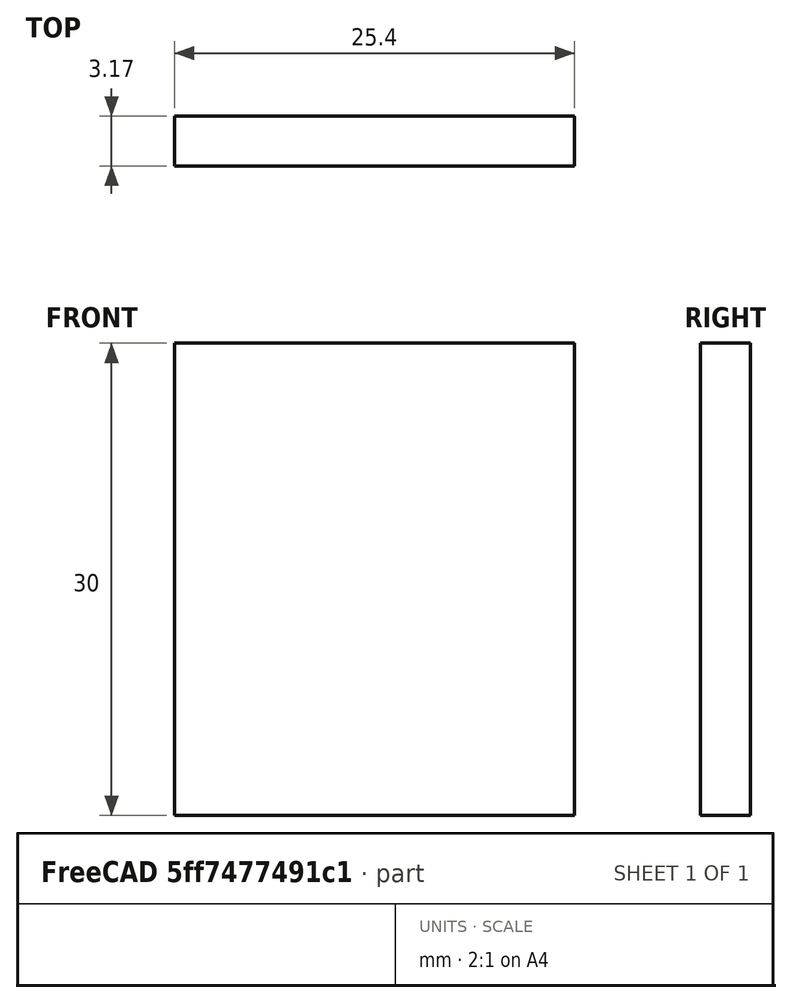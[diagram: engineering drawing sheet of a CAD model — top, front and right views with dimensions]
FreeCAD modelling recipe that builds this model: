
FCSTD DOCUMENT  (FreeCAD 1.0R39109 (Git))
Label: Sample
License: All rights reserved
LicenseURL: https://en.wikipedia.org/wiki/All_rights_reserved
objects: PartDesign::CoordinateSystem×2, App::DocumentObjectGroup×2, Sketcher::SketchObject×1, PartDesign::Pad×1, PartDesign::Body×1, App::FeaturePython×1, App::Part×1
note: 8 computed .brp shape members not serialized (recipe doc carries the construction recipe); baked Part::Feature solids carry a one-line shape summary decoded from their .brp

FEATURE [Sketcher::SketchObject] Sketch
  ArcFitTolerance = 0
  AttachmentSupport = -> [XY_Plane]
  FullyConstrained = true
  MakeInternals = false
  MapMode = 5
  sketch-geometry (4):
    g0: LineSegment StartX=-12.7 StartY=1.5825 StartZ=0 EndX=12.7 EndY=1.5825 EndZ=0
    g1: LineSegment StartX=12.7 StartY=1.5825 StartZ=0 EndX=12.7 EndY=-1.5875 EndZ=0
    g2: LineSegment StartX=12.7 StartY=-1.5875 StartZ=0 EndX=-12.7 EndY=-1.5875 EndZ=0
    g3: LineSegment StartX=-12.7 StartY=-1.5875 StartZ=0 EndX=-12.7 EndY=1.5825 EndZ=0
  constraints (12):
    c: Coincident(g0,g1)
    c: Coincident(g1,g2)
    c: Coincident(g2,g3)
    c: Coincident(g3,g0)
    c: Horizontal(g0)
    c: Horizontal(g2)
    c: Vertical(g1)
    c: Vertical(g3)
    c: DistanceX(g2,g2) = 25.4
    c: DistanceX(g-1,g1) = 12.7
    c: DistanceY(g1,g1) = -3.17
    c: DistanceY(g1,g-1) = 1.5875
FEATURE [PartDesign::Pad] Pad
  Direction = (0,0,1)
  Length = 30
  Length2 = 10
  Profile = -> Sketch
  ReferenceAxis = -> Sketch [N_Axis]
  Suppressed = false
  Type = 0
FEATURE [PartDesign::Body] Body
  AllowCompound = false
  Group = -> [Sketch,Pad]
  Origin = -> Origin
  Tip = -> Pad
FEATURE [PartDesign::CoordinateSystem] LCS_Origin
  AttacherType = Attacher::AttachEngine3D
  AttachmentSupport = -> [X_Axis001]
  MapMode = 2
FEATURE [App::DocumentObjectGroup] Constraints
FEATURE [App::FeaturePython] Variables  # WARN: FeaturePython — macro-defined, semantics opaque (R4)
  Type = App::PropertyContainer
FEATURE [App::DocumentObjectGroup] Configurations
FEATURE [PartDesign::CoordinateSystem] LCS_1  label="45_deg"
  AttacherType = Attacher::AttachEngine3D
  Placement = pos=(0,0,0) rot=(0,0,1;0.785398rad)
FEATURE [App::Part] Assembly  label="Sample"
  AssemblyType = Part::Link
  Group = -> [LCS_Origin,Constraints,Variables,Configurations,Body,LCS_1]
  Origin = -> Origin001
  Type = Assembly
